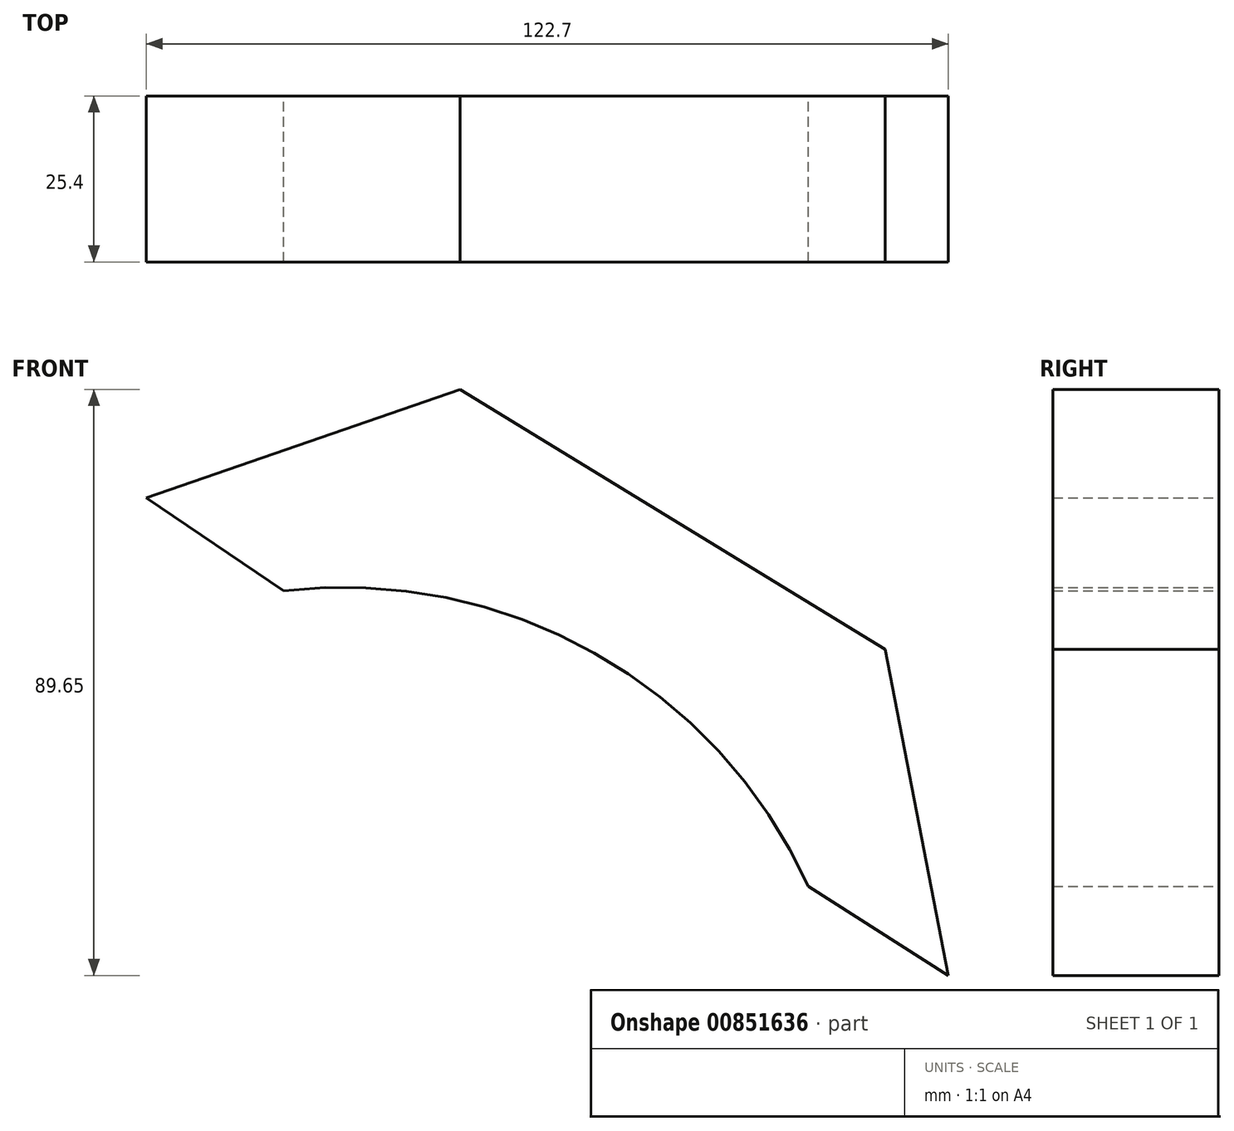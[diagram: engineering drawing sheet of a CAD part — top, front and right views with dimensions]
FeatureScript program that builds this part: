
annotation { "Feature Type Name" : "Feature", "Feature Type Description" : "" }
export const myFeature = defineFeature(function(context is Context, id is Id, definition is map)
    precondition{}
    {
        {
            var Q0;
            Q0=qCreatedBy(makeId("Front.planeOp"),FACE);
            var sketch = newSketch(context, id + "F0", { "sketchPlane" : qUnion([Q0])});
            skLineSegment(sketch, "E0", {"start": v(2.53, -40.31) * mm, "end": v(23.97, -53.93) * mm});
            skLineSegment(sketch, "E1", {"start": v(23.97, -53.93) * mm, "end": v(14.29, -4.06) * mm});
            skLineSegment(sketch, "E2", {"start": v(14.29, -4.06) * mm, "end": v(-50.71, 35.72) * mm});
            skLineSegment(sketch, "E3", {"start": v(-50.71, 35.72) * mm, "end": v(-98.73, 19.14) * mm});
            skLineSegment(sketch, "E4", {"start": v(-98.73, 19.14) * mm, "end": v(-77.7, 4.9) * mm});
            skArc(sketch, "E5", {"start": v(2.53, -40.31) * mm, "mid": v(-30.2, -4.6) * mm, "end": v(-77.7, 4.9) * mm});
            skSolve(sketch);
        }
        {
            var Q0;
            Q0 = qSketchRegion(id + "F0", true);
            extrude(context, id + "F1", {"entities" : qUnion([Q0]), "depth" : 25.4 * mm, "offsetDistance" : 25.4 * mm});
        }
    });
